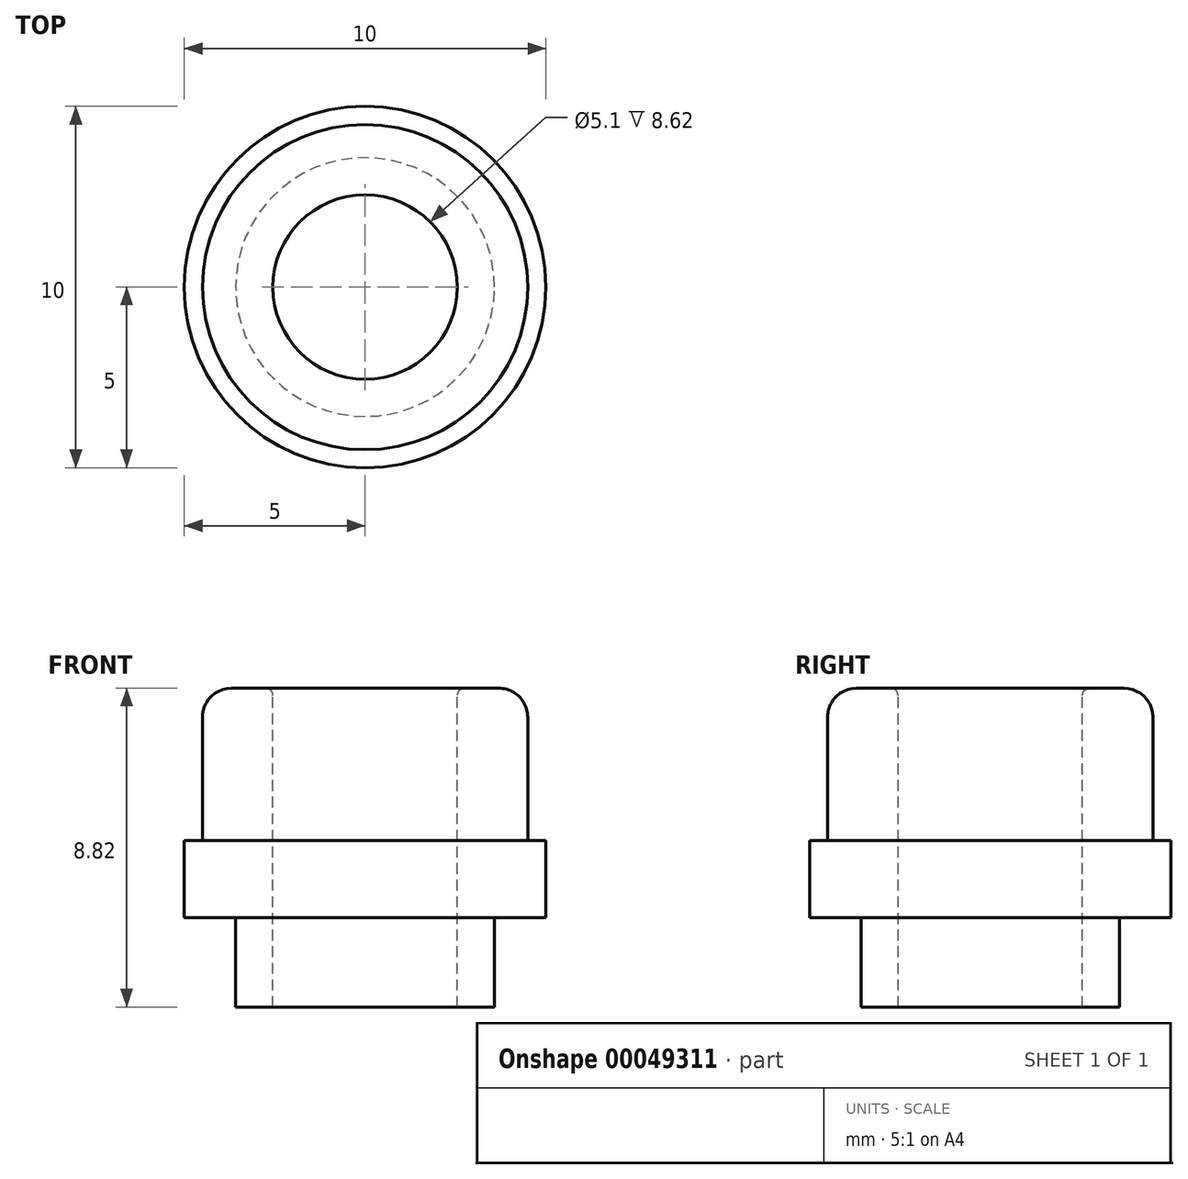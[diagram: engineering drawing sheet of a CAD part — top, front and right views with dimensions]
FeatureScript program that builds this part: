
annotation { "Feature Type Name" : "Feature", "Feature Type Description" : "" }
export const myFeature = defineFeature(function(context is Context, id is Id, definition is map)
    precondition{}
    {
        {
            var Q0;
            Q0=qCreatedBy(makeId("Front.planeOp"),FACE);
            var sketch = newSketch(context, id + "F0", { "sketchPlane" : qUnion([Q0])});
            skLineSegment(sketch, "E0", {"start": v(0, 5.54) * mm, "end": v(0, -7.32) * mm, "construction": true});
            skLineSegment(sketch, "E1", {"start": v(-2.55, 6.35) * mm, "end": v(-4.5, 6.35) * mm});
            skLineSegment(sketch, "E2", {"start": v(-4.5, 6.35) * mm, "end": v(-4.5, 2.13) * mm});
            skLineSegment(sketch, "E3", {"start": v(-4.5, 2.13) * mm, "end": v(-5, 2.13) * mm});
            skLineSegment(sketch, "E4", {"start": v(-5, 2.13) * mm, "end": v(-5, 0) * mm});
            skLineSegment(sketch, "E5", {"start": v(-5, 0) * mm, "end": v(-3.58, 0) * mm});
            skLineSegment(sketch, "E6", {"start": v(-3.58, 0) * mm, "end": v(-3.58, -2.47) * mm});
            skLineSegment(sketch, "E7", {"start": v(-3.58, -2.47) * mm, "end": v(-2.55, -2.47) * mm});
            skLineSegment(sketch, "E8", {"start": v(-2.55, -2.47) * mm, "end": v(-2.55, 6.35) * mm});
            skSolve(sketch);
        }
        {
            var Q0;
            Q0 = qSketchRegion(id + "F0", true);
            var Q1;
            Q1=sQuery(id+"F0.wireOp",EDGE,"E0");
            revolve(context, id + "F1", {"entities" : qUnion([Q0]), "axis" : qUnion([Q1]), "revolveType" : RevolveType.FULL});
        }
        {
            var Q0;
            Q0=makeQuery(id+"F1.opRevolve","SWEPT_EDGE",EDGE,{"disambiguationData":[OSD([sQuery(id+"F0.wireOp",EDGE,"E1"),sQuery(id+"F0.wireOp",EDGE,"E2")])]});
            fillet(context, id + "F2", {"entities" : qUnion([Q0]), "radius" : 0.8 * mm, "tangentPropagation" : true, "allowEdgeOverflow" : false});
        }
        {
            var Q0;
            Q0=makeQuery(id+"F1.opRevolve","SWEPT_EDGE",EDGE,{"disambiguationData":[OSD([sQuery(id+"F0.wireOp",EDGE,"E1"),sQuery(id+"F0.wireOp",EDGE,"E8")])]});
            fillet(context, id + "F3", {"entities" : qUnion([Q0]), "radius" : 0.2 * mm, "tangentPropagation" : true, "allowEdgeOverflow" : false});
        }
    });
